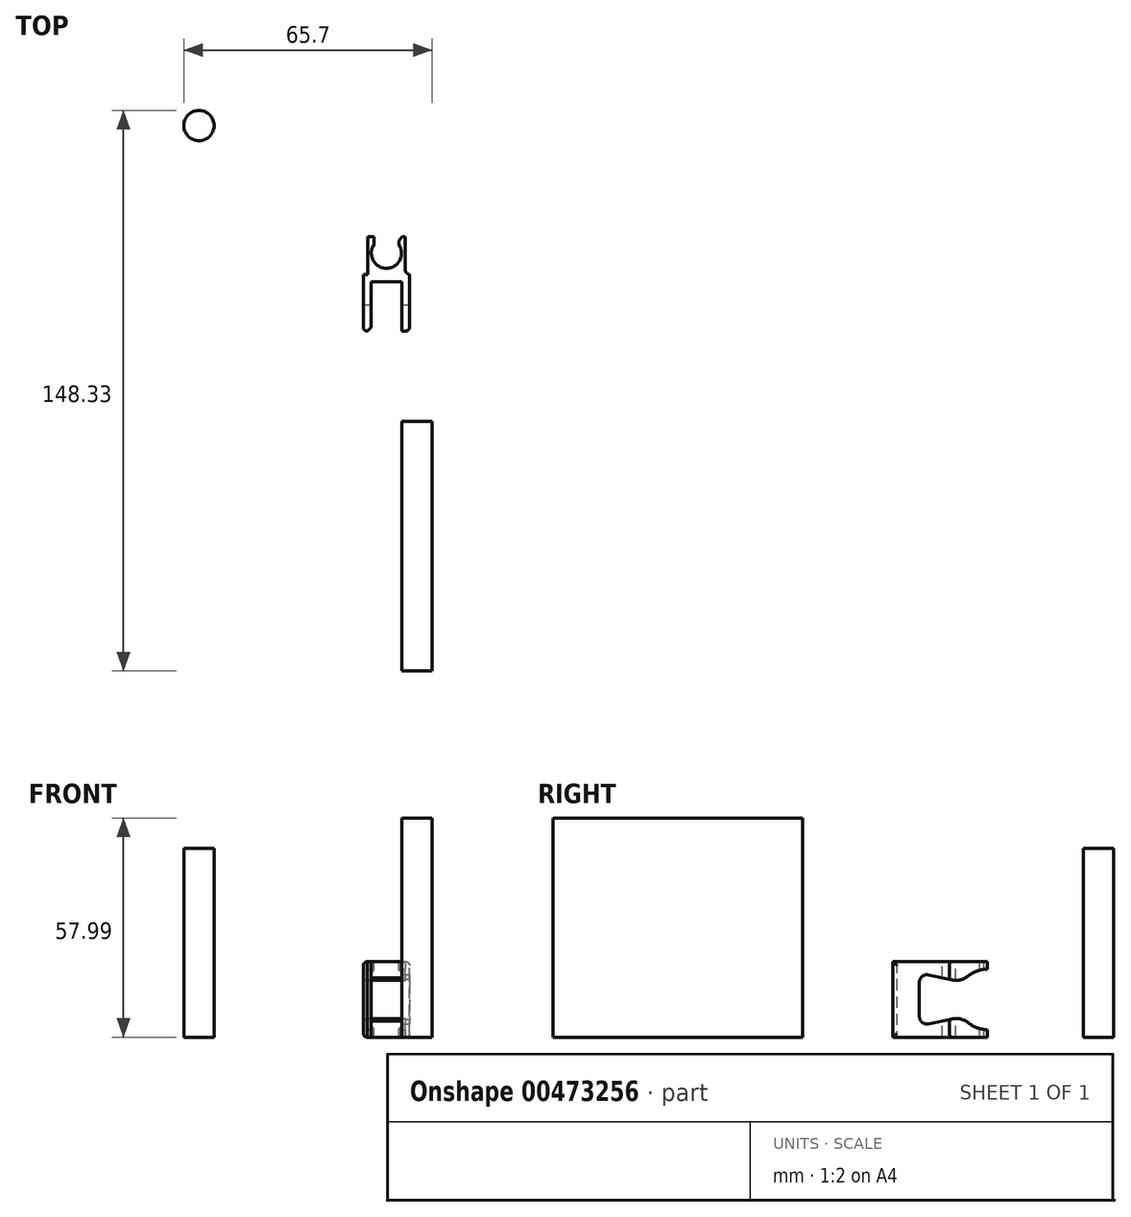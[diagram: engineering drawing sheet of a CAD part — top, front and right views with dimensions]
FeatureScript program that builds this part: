
annotation { "Feature Type Name" : "Feature", "Feature Type Description" : "" }
export const myFeature = defineFeature(function(context is Context, id is Id, definition is map)
    precondition{}
    {
        {
            var Q0;
            Q0=qCreatedBy(makeId("Front.planeOp"),FACE);
            var sketch = newSketch(context, id + "F0", { "sketchPlane" : qUnion([Q0])});
            skLineSegment(sketch, "E0.bottom", {"start": v(0, 0) * mm, "end": v(-8.2, 0) * mm});
            skLineSegment(sketch, "E0.top", {"start": v(0, 20) * mm, "end": v(-8.2, 20) * mm});
            skLineSegment(sketch, "E0.left", {"start": v(0, 0) * mm, "end": v(0, 20) * mm});
            skLineSegment(sketch, "E0.right", {"start": v(-8.2, 0) * mm, "end": v(-8.2, 20) * mm});
            skLineSegment(sketch, "E1", {"start": v(-10.2, 0) * mm, "end": v(-10.2, 20) * mm});
            skLineSegment(sketch, "E2", {"start": v(2, 0) * mm, "end": v(2, 20) * mm});
            skLineSegment(sketch, "E3", {"start": v(-10.2, 20) * mm, "end": v(2, 20) * mm});
            skLineSegment(sketch, "E4", {"start": v(2, 0) * mm, "end": v(-10.2, 0) * mm});
            skSolve(sketch);
        }
        {
            var Q0;
            {var subQ0=sQuery(id+"F0.wireOp",EDGE,"E0.bottom");var subQ2=sQuery(id+"F0.wireOp",EDGE,"E0.left");var subQ3=makeQuery(id+"F0.imprint","IMPRINT",EDGE,{"derivedFrom":subQ2});var subQ4=sQuery(id+"F0.wireOp",EDGE,"E0.right");var subQ5=makeQuery(id+"F0.imprint","IMPRINT",EDGE,{"derivedFrom":subQ4});Q0=qUnion([makeQuery(id+"F0.imprint","IMPRINT",FACE,{"disambiguationData":[TD([[subQ3,-1.0]])]}),makeQuery(id+"F0.imprint","IMPRINT",FACE,{"disambiguationData":[TD([[subQ5,1.0]])]}),makeQuery(id+"F0.imprint","IMPRINT",FACE,{"disambiguationData":[TD([[makeQuery(id+"F0.imprint","IMPRINT",EDGE,{"derivedFrom":subQ0}),-1.0]])]})]);}
            extrude(context, id + "F1", {"entities" : qUnion([Q0]), "oppositeDirection" : true, "depth" : 15 * mm, "offsetDistance" : 25 * mm});
        }
        {
            var Q0;
            Q0=makeQuery(id+"F0.imprint","IMPRINT",FACE,{"disambiguationData":[TD([[makeQuery(id+"F0.imprint","IMPRINT",EDGE,{"derivedFrom":sQuery(id+"F0.wireOp",EDGE,"E0.bottom")}),-1.0]])]});
            extrude(context, id + "F2", {"entities" : qUnion([Q0]), "operationType" : NewBodyOperationType.REMOVE, "oppositeDirection" : true, "depth" : 13 * mm, "offsetDistance" : 25 * mm});
        }
        {
            var Q0;
            Q0=makeQuery(id+"F1.opExtrude","CAP_FACE",FACE,{"disambiguationData":[OSD([sQuery(id+"F0.wireOp",EDGE,"E0.bottom"),sQuery(id+"F0.wireOp",EDGE,"E0.top"),sQuery(id+"F0.wireOp",EDGE,"E1"),sQuery(id+"F0.wireOp",EDGE,"E2"),sQuery(id+"F0.wireOp",EDGE,"E3"),sQuery(id+"F0.wireOp",EDGE,"E4")])],"isStart":false});
            var sketch = newSketch(context, id + "F3", { "sketchPlane" : qUnion([Q0])});
            skLineSegment(sketch, "E5.bottom", {"start": v(-0.9, 20) * mm, "end": v(9.1, 20) * mm});
            skLineSegment(sketch, "E5.top", {"start": v(-0.9, 0) * mm, "end": v(9.1, 0) * mm});
            skLineSegment(sketch, "E5.left", {"start": v(-0.9, 20) * mm, "end": v(-0.9, 0) * mm});
            skLineSegment(sketch, "E5.right", {"start": v(9.1, 20) * mm, "end": v(9.1, 0) * mm});
            skLineSegment(sketch, "E6", {"start": v(-2, 10) * mm, "end": v(-0.9, 10) * mm, "construction": true});
            skLineSegment(sketch, "E7", {"start": v(9.1, 10) * mm, "end": v(10.2, 10) * mm, "construction": true});
            skSolve(sketch);
        }
        {
            var Q0;
            Q0=makeQuery(id+"F3.imprint","IMPRINT",FACE,{"disambiguationData":[TD([[makeQuery(id+"F3.imprint","IMPRINT",EDGE,{"derivedFrom":sQuery(id+"F3.wireOp",EDGE,"E5.bottom")}),1.0]])]});
            extrude(context, id + "F4", {"entities" : qUnion([Q0]), "operationType" : NewBodyOperationType.ADD, "depth" : 10 * mm, "offsetDistance" : 25 * mm});
        }
        {
            var Q0;
            Q0=makeQuery(id+"F4.opExtrude","CAP_EDGE",EDGE,{"disambiguationData":[OSD([sQuery(id+"F3.wireOp",EDGE,"E5.right")])],"isStart":true});
            var Q1;
            Q1=makeQuery(id+"F4.opExtrude","CAP_EDGE",EDGE,{"disambiguationData":[OSD([sQuery(id+"F3.wireOp",EDGE,"E5.left")])],"isStart":true});
            fillet(context, id + "F5", {"entities" : qUnion([Q0, Q1]), "radius" : 1.25 * mm, "tangentPropagation" : true, "allowEdgeOverflow" : false});
        }
        {
            var Q0;
            Q0=makeQuery(id+"F4.boolean.opBoolean","MERGE",FACE,{"derivedFrom":[makeQuery(id+"F1.opExtrude","SWEPT_FACE",FACE,{"disambiguationData":[OSD([sQuery(id+"F0.wireOp",EDGE,"E0.top"),sQuery(id+"F0.wireOp",EDGE,"E3")])]}),makeQuery(id+"F4.opExtrude","SWEPT_FACE",FACE,{"disambiguationData":[OSD([sQuery(id+"F3.wireOp",EDGE,"E5.bottom")])]})]});
            var sketch = newSketch(context, id + "F6", { "sketchPlane" : qUnion([Q0])});
            skLineSegment(sketch, "E8", {"start": v(0.9, 16.24) * mm, "end": v(-9.1, 16.24) * mm, "construction": true});
            skLineSegment(sketch, "E9", {"start": v(-9.1, 16.24) * mm, "end": v(0.9, 25) * mm, "construction": true});
            skLineSegment(sketch, "E10", {"start": v(0.9, 16.24) * mm, "end": v(-9.1, 25) * mm, "construction": true});
            skArc(sketch, "E11", {"start": v(-7.35, 22.95) * mm, "mid": v(-4.1, 16.62) * mm, "end": v(-0.85, 22.95) * mm});
            skLineSegment(sketch, "E12.bottom", {"start": v(-7.35, 27.7) * mm, "end": v(-0.85, 27.7) * mm});
            skLineSegment(sketch, "E12.left", {"start": v(-7.35, 27.7) * mm, "end": v(-7.35, 22.95) * mm});
            skLineSegment(sketch, "E12.right", {"start": v(-0.85, 27.7) * mm, "end": v(-0.85, 22.95) * mm});
            skPoint(sketch, "E12.top.end.orphan", {"position": v(-0.85, 13.54) * mm});
            skPoint(sketch, "E13.orphan", {"position": v(-7.35, 13.54) * mm});
            skSolve(sketch);
        }
        {
            var Q0;
            {var subQ0=sQuery(id+"F6.wireOp",EDGE,"E11");Q0=makeQuery(id+"F6.imprint","IMPRINT",FACE,{"disambiguationData":[TD([[makeQuery(id+"F6.imprint","IMPRINT",EDGE,{"derivedFrom":subQ0}),1.0]])]});}
            extrude(context, id + "F7", {"entities" : qUnion([Q0]), "operationType" : NewBodyOperationType.REMOVE, "endBound" : BoundingType.THROUGH_ALL, "oppositeDirection" : true, "depth" : 25 * mm, "offsetDistance" : 25 * mm});
        }
        {
            var Q0;
            Q0=makeQuery(id+"F7.boolean.opBoolean","COPY",EDGE,{"derivedFrom":makeQuery(id+"F7.opExtrude","SWEPT_EDGE",EDGE,{"disambiguationData":[OSD([sQuery(id+"F3.wireOp",EDGE,"E5.bottom"),sQuery(id+"F6.wireOp",EDGE,"E12.right")])]})});
            var Q1;
            Q1=makeQuery(id+"F7.boolean.opBoolean","COPY",EDGE,{"derivedFrom":makeQuery(id+"F7.opExtrude","SWEPT_EDGE",EDGE,{"disambiguationData":[OSD([sQuery(id+"F3.wireOp",EDGE,"E5.bottom"),sQuery(id+"F6.wireOp",EDGE,"E12.left")])]})});
            chamfer(context, id + "F8", {"entities" : qUnion([Q0, Q1]), "width" : 1 * mm, "tangentPropagation" : true});
        }
        {
            var Q0;
            Q0=makeQuery(id+"F1.opExtrude","SWEPT_EDGE",EDGE,{"disambiguationData":[OSD([sQuery(id+"F0.wireOp",EDGE,"E1"),sQuery(id+"F0.wireOp",EDGE,"E3")])]});
            var Q1;
            Q1=makeQuery(id+"F1.opExtrude","SWEPT_EDGE",EDGE,{"disambiguationData":[OSD([sQuery(id+"F0.wireOp",EDGE,"E1"),sQuery(id+"F0.wireOp",EDGE,"E4")])]});
            var Q2;
            Q2=makeQuery(id+"F1.opExtrude","CAP_EDGE",EDGE,{"disambiguationData":[OSD([sQuery(id+"F0.wireOp",EDGE,"E1")])],"isStart":true});
            var Q3;
            Q3=makeQuery(id+"F1.opExtrude","SWEPT_EDGE",EDGE,{"disambiguationData":[OSD([sQuery(id+"F0.wireOp",EDGE,"E2"),sQuery(id+"F0.wireOp",EDGE,"E3")])]});
            var Q4;
            Q4=makeQuery(id+"F1.opExtrude","SWEPT_EDGE",EDGE,{"disambiguationData":[OSD([sQuery(id+"F0.wireOp",EDGE,"E2"),sQuery(id+"F0.wireOp",EDGE,"E4")])]});
            var Q5;
            Q5=makeQuery(id+"F1.opExtrude","CAP_EDGE",EDGE,{"disambiguationData":[OSD([sQuery(id+"F0.wireOp",EDGE,"E2")])],"isStart":true});
            fillet(context, id + "F9", {"entities" : qUnion([Q0, Q1, Q2, Q3, Q4, Q5]), "radius" : 1 * mm, "tangentPropagation" : true, "allowEdgeOverflow" : false});
        }
        {
            var Q0;
            Q0=makeQuery(id+"F2.boolean.opBoolean","COPY",EDGE,{"derivedFrom":makeQuery(id+"F2.opExtrude","CAP_EDGE",EDGE,{"disambiguationData":[OSD([sQuery(id+"F0.wireOp",EDGE,"E0.left")])],"isStart":true})});
            var Q1;
            Q1=makeQuery(id+"F2.boolean.opBoolean","COPY",EDGE,{"derivedFrom":makeQuery(id+"F2.opExtrude","CAP_EDGE",EDGE,{"disambiguationData":[OSD([sQuery(id+"F0.wireOp",EDGE,"E0.right")])],"isStart":true})});
            chamfer(context, id + "F10", {"entities" : qUnion([Q0, Q1]), "width" : 1 * mm, "tangentPropagation" : true});
        }
        {
            var Q0;
            Q0=qCreatedBy(makeId("Top.planeOp"),FACE);
            var sketch = newSketch(context, id + "F11", { "sketchPlane" : qUnion([Q0])});
            skCircle(sketch, "E14", {"center": v(-53.7, 54.4) * mm, "radius": 4 * mm});
            skSolve(sketch);
        }
        {
            var Q0;
            Q0=makeQuery(id+"F11.imprint","IMPRINT",FACE,{"disambiguationData":[TD([[makeQuery(id+"F11.imprint","IMPRINT",EDGE,{"derivedFrom":sQuery(id+"F11.wireOp",EDGE,"E14")}),1.0]])]});
            extrude(context, id + "F12", {"entities" : qUnion([Q0]), "depth" : 50 * mm, "offsetDistance" : 25 * mm});
        }
        {
            var Q0;
            Q0=qCreatedBy(makeId("Right.planeOp"),FACE);
            var sketch = newSketch(context, id + "F13", { "sketchPlane" : qUnion([Q0])});
            skLineSegment(sketch, "E15.bottom", {"start": v(-23.85, 0) * mm, "end": v(-89.93, 0) * mm});
            skLineSegment(sketch, "E15.top", {"start": v(-23.85, 57.99) * mm, "end": v(-89.93, 57.99) * mm});
            skLineSegment(sketch, "E15.left", {"start": v(-23.85, 0) * mm, "end": v(-23.85, 57.99) * mm});
            skLineSegment(sketch, "E15.right", {"start": v(-89.93, 0) * mm, "end": v(-89.93, 57.99) * mm});
            skSolve(sketch);
        }
        {
            var Q0;
            Q0=makeQuery(id+"F13.imprint","IMPRINT",FACE,{"disambiguationData":[TD([[makeQuery(id+"F13.imprint","IMPRINT",EDGE,{"derivedFrom":sQuery(id+"F13.wireOp",EDGE,"E15.bottom")}),-1.0]])]});
            extrude(context, id + "F14", {"entities" : qUnion([Q0]), "depth" : 8 * mm, "offsetDistance" : 25 * mm});
        }
        {
            var Q0;
            Q0=makeQuery(id+"F1.opExtrude","SWEPT_FACE",FACE,{"disambiguationData":[OSD([sQuery(id+"F0.wireOp",EDGE,"E2")])]});
            var sketch = newSketch(context, id + "F15", { "sketchPlane" : qUnion([Q0])});
            skLineSegment(sketch, "E16", {"start": v(9.41, 16.5) * mm, "end": v(15.73, 15.16) * mm});
            skLineSegment(sketch, "E17", {"start": v(15.73, 4.84) * mm, "end": v(9.41, 3.5) * mm});
            skLineSegment(sketch, "E18", {"start": v(7, 14.54) * mm, "end": v(7, 5.46) * mm});
            skArc(sketch, "E19", {"start": v(19.93, 3.81) * mm, "mid": v(33, 10) * mm, "end": v(19.93, 16.19) * mm});
            skPoint(sketch, "E20.orphan", {"position": v(40.27, 10) * mm});
            skPoint(sketch, "E21.visualSharp", {"position": v(18.45, 14.6) * mm});
            skArc(sketch, "E21.filletArc", {"start": v(15.73, 15.16) * mm, "mid": v(17.95, 15.2) * mm, "end": v(19.93, 16.19) * mm});
            skPoint(sketch, "E22.visualSharp", {"position": v(18.45, 5.4) * mm});
            skArc(sketch, "E22.filletArc", {"start": v(19.93, 3.81) * mm, "mid": v(17.95, 4.8) * mm, "end": v(15.73, 4.84) * mm});
            skPoint(sketch, "E23.visualSharp", {"position": v(7, 17) * mm});
            skArc(sketch, "E23.filletArc", {"start": v(9.41, 16.5) * mm, "mid": v(7.74, 16.09) * mm, "end": v(7, 14.54) * mm});
            skPoint(sketch, "E24.visualSharp", {"position": v(7, 3) * mm});
            skArc(sketch, "E24.filletArc", {"start": v(7, 5.46) * mm, "mid": v(7.74, 3.91) * mm, "end": v(9.41, 3.5) * mm});
            skSolve(sketch);
        }
        {
            var Q0;
            {var subQ0=sQuery(id+"F15.wireOp",EDGE,"E18");Q0=makeQuery(id+"F15.imprint","IMPRINT",FACE,{"disambiguationData":[TD([[makeQuery(id+"F15.imprint","IMPRINT",EDGE,{"derivedFrom":subQ0}),1.0]])]});}
            var Q1;
            {var subQ0=sQuery(id+"F15.wireOp",EDGE,"E17");var subQ1=sQuery(id+"F15.wireOp",EDGE,"E16");var subQ2=makeQuery(id+"F15.imprint","INTERSECT",VERTEX,{"derivedFrom":[subQ1,subQ0]});Q1=makeQuery(id+"F15.imprint","IMPRINT",FACE,{"disambiguationData":[TD([[makeQuery(id+"F15.imprint","IMPRINT",EDGE,{"disambiguationData":[TD([[subQ2,1.0]])],"derivedFrom":subQ1}),-1.0]])]});}
            var Q2;
            Q2=makeQuery(id+"F15.imprint","IMPRINT",FACE,{"disambiguationData":[TD([[makeQuery(id+"F15.imprint","IMPRINT",EDGE,{"derivedFrom":sQuery(id+"F15.wireOp",EDGE,"E19")}),1.0]])]});
            extrude(context, id + "F16", {"entities" : qUnion([Q0, Q1, Q2]), "operationType" : NewBodyOperationType.REMOVE, "oppositeDirection" : true, "depth" : 25 * mm, "offsetDistance" : 25 * mm});
        }
    });
